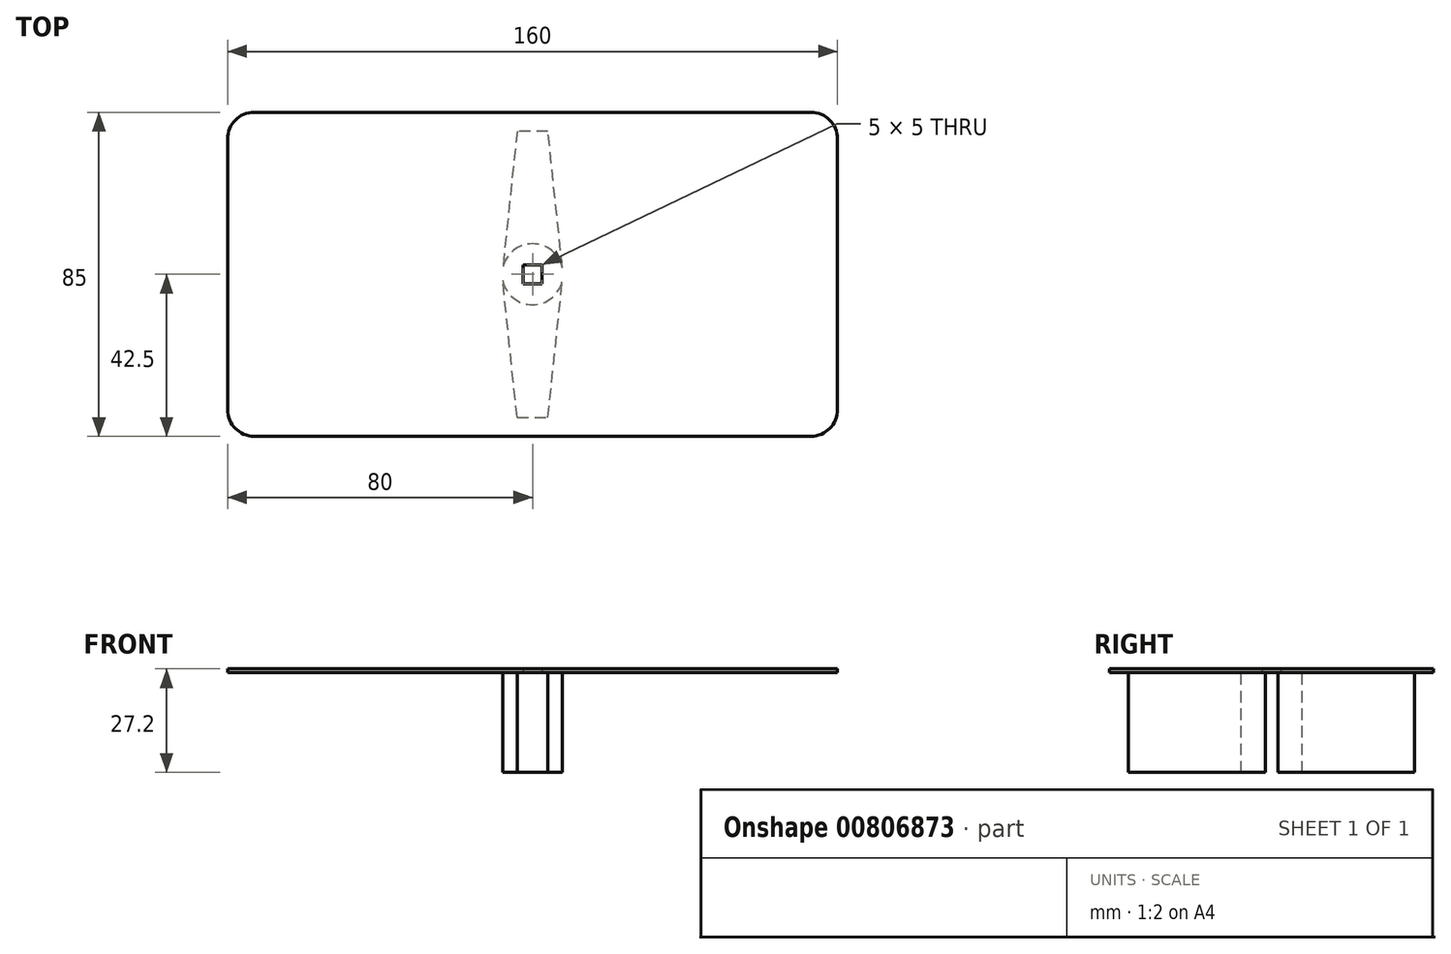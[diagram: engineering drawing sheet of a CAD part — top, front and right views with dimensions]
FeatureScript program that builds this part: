
annotation { "Feature Type Name" : "Feature", "Feature Type Description" : "" }
export const myFeature = defineFeature(function(context is Context, id is Id, definition is map)
    precondition{}
    {
        {
            var Q0;
            Q0=qCreatedBy(makeId("Top.planeOp"),FACE);
            var sketch = newSketch(context, id + "F0", { "sketchPlane" : qUnion([Q0])});
            skLineSegment(sketch, "E0.bottom", {"start": v(80, -42.5) * mm, "end": v(-80, -42.5) * mm});
            skLineSegment(sketch, "E0.top", {"start": v(80, 42.5) * mm, "end": v(-80, 42.5) * mm});
            skLineSegment(sketch, "E0.left", {"start": v(80, -42.5) * mm, "end": v(80, 42.5) * mm});
            skLineSegment(sketch, "E0.right", {"start": v(-80, -42.5) * mm, "end": v(-80, 42.5) * mm});
            skPoint(sketch, "E0.middle", {"position": v(0, 0) * mm});
            skCircle(sketch, "E1", {"center": v(0, 0) * mm, "radius": 8 * mm});
            skLineSegment(sketch, "E2", {"start": v(80, 42.5) * mm, "end": v(80, 35.5) * mm});
            skLineSegment(sketch, "E3", {"start": v(80, 42.5) * mm, "end": v(73, 42.5) * mm});
            skArc(sketch, "E4", {"start": v(80, 35.5) * mm, "mid": v(77.95, 40.45) * mm, "end": v(73, 42.5) * mm});
            skLineSegment(sketch, "E5", {"start": v(80, -42.5) * mm, "end": v(80, -35.5) * mm});
            skLineSegment(sketch, "E6", {"start": v(80, -42.5) * mm, "end": v(73, -42.5) * mm});
            skArc(sketch, "E7", {"start": v(73, -42.5) * mm, "mid": v(77.95, -40.45) * mm, "end": v(80, -35.5) * mm});
            skLineSegment(sketch, "E8", {"start": v(-80, -42.5) * mm, "end": v(-73, -42.5) * mm});
            skLineSegment(sketch, "E9", {"start": v(-80, -42.5) * mm, "end": v(-80, -35.5) * mm});
            skArc(sketch, "E10", {"start": v(-80, -35.5) * mm, "mid": v(-77.95, -40.45) * mm, "end": v(-73, -42.5) * mm});
            skLineSegment(sketch, "E11", {"start": v(-80, 42.5) * mm, "end": v(-80, 35.5) * mm});
            skLineSegment(sketch, "E12", {"start": v(-80, 42.5) * mm, "end": v(-73, 42.5) * mm});
            skArc(sketch, "E13", {"start": v(-73, 42.5) * mm, "mid": v(-77.95, 40.45) * mm, "end": v(-80, 35.5) * mm});
            skSolve(sketch);
        }
        {
            var Q0;
            Q0=makeQuery(id+"F0.imprint","IMPRINT",FACE,{"disambiguationData":[TD([[makeQuery(id+"F0.imprint","IMPRINT",EDGE,{"derivedFrom":sQuery(id+"F0.wireOp",EDGE,"E1")}),1.0]])]});
            var Q1;
            Q1=makeQuery(id+"F0.imprint","IMPRINT",FACE,{"disambiguationData":[TD([[makeQuery(id+"F0.imprint","IMPRINT",EDGE,{"derivedFrom":sQuery(id+"F0.wireOp",EDGE,"E1")}),-1.0]])]});
            extrude(context, id + "F1", {"entities" : qUnion([Q0, Q1]), "depth" : 1 * mm, "offsetDistance" : 25 * mm});
        }
        {
            var Q0;
            Q0=makeQuery(id+"F1.opExtrude","CAP_FACE",FACE,{"disambiguationData":[OSD([sQuery(id+"F0.wireOp",EDGE,"E0.bottom"),sQuery(id+"F0.wireOp",EDGE,"E0.top"),sQuery(id+"F0.wireOp",EDGE,"E0.left"),sQuery(id+"F0.wireOp",EDGE,"E0.right"),sQuery(id+"F0.wireOp",EDGE,"E4"),sQuery(id+"F0.wireOp",EDGE,"E7"),sQuery(id+"F0.wireOp",EDGE,"E10"),sQuery(id+"F0.wireOp",EDGE,"E13")])],"isStart":true});
            var sketch = newSketch(context, id + "F2", { "sketchPlane" : qUnion([Q0])});
            skCircle(sketch, "E14", {"center": v(0, 0) * mm, "radius": 8 * mm});
            skSolve(sketch);
        }
        {
            var Q0;
            Q0=makeQuery(id+"F1.opExtrude","CAP_FACE",FACE,{"disambiguationData":[OSD([sQuery(id+"F0.wireOp",EDGE,"E0.bottom"),sQuery(id+"F0.wireOp",EDGE,"E0.top"),sQuery(id+"F0.wireOp",EDGE,"E0.left"),sQuery(id+"F0.wireOp",EDGE,"E0.right"),sQuery(id+"F0.wireOp",EDGE,"E4"),sQuery(id+"F0.wireOp",EDGE,"E7"),sQuery(id+"F0.wireOp",EDGE,"E10"),sQuery(id+"F0.wireOp",EDGE,"E13")])],"isStart":true});
            var sketch = newSketch(context, id + "F3", { "sketchPlane" : qUnion([Q0])});
            skCircle(sketch, "E15", {"center": v(0, 0) * mm, "radius": 8 * mm});
            skLineSegment(sketch, "E16", {"start": v(-8, 0) * mm, "end": v(-8, 25) * mm});
            skLineSegment(sketch, "E17", {"start": v(8, 0) * mm, "end": v(8, 25) * mm});
            skLineSegment(sketch, "E18", {"start": v(8, 25) * mm, "end": v(-8, 25) * mm});
            skLineSegment(sketch, "E19", {"start": v(-8, 0) * mm, "end": v(-8, -15) * mm});
            skLineSegment(sketch, "E20", {"start": v(8, 0) * mm, "end": v(8, -15) * mm});
            skLineSegment(sketch, "E21", {"start": v(8, -15) * mm, "end": v(-8, -15) * mm});
            skLineSegment(sketch, "E22", {"start": v(3.08, -15) * mm, "end": v(4.02, -10.14) * mm});
            skLineSegment(sketch, "E23", {"start": v(8, 0) * mm, "end": v(3.48, -43) * mm});
            skLineSegment(sketch, "E24", {"start": v(8, -15) * mm, "end": v(8, -42.5) * mm});
            skLineSegment(sketch, "E25", {"start": v(8, -42.5) * mm, "end": v(3.53, -42.5) * mm});
            skLineSegment(sketch, "E26", {"start": v(8, 25) * mm, "end": v(8, 42.5) * mm});
            skLineSegment(sketch, "E27", {"start": v(8, 42.5) * mm, "end": v(3.53, 42.5) * mm});
            skLineSegment(sketch, "E28", {"start": v(3.53, 42.5) * mm, "end": v(8, 0) * mm});
            skLineSegment(sketch, "E29", {"start": v(-8, 25) * mm, "end": v(-8, 42.5) * mm});
            skLineSegment(sketch, "E30", {"start": v(-8, 42.5) * mm, "end": v(-3.53, 42.5) * mm});
            skLineSegment(sketch, "E31", {"start": v(-3.53, 42.5) * mm, "end": v(-8, 0) * mm});
            skLineSegment(sketch, "E32", {"start": v(-8, -15) * mm, "end": v(-8, -42.5) * mm});
            skLineSegment(sketch, "E33", {"start": v(-8, -42.5) * mm, "end": v(-3.53, -42.5) * mm});
            skLineSegment(sketch, "E34", {"start": v(-3.53, -42.5) * mm, "end": v(-8, 0) * mm});
            skLineSegment(sketch, "E35", {"start": v(-8, -42.5) * mm, "end": v(-8, -37.5) * mm});
            skLineSegment(sketch, "E36", {"start": v(8, -42.5) * mm, "end": v(8, -37.5) * mm});
            skLineSegment(sketch, "E37", {"start": v(8, -37.5) * mm, "end": v(-8, -37.5) * mm});
            skLineSegment(sketch, "E38", {"start": v(8, 42.5) * mm, "end": v(8, 37.5) * mm});
            skLineSegment(sketch, "E39", {"start": v(-8, 42.5) * mm, "end": v(-8, 37.5) * mm});
            skLineSegment(sketch, "E40", {"start": v(-8, 37.5) * mm, "end": v(8, 37.5) * mm});
            skLineSegment(sketch, "E41", {"start": v(-8, 1.41) * mm, "end": v(-8, -1.52) * mm});
            skLineSegment(sketch, "E42", {"start": v(8, 2.1) * mm, "end": v(8, -1.7) * mm});
            skSolve(sketch);
        }
        {
            var Q0;
            Q0=makeQuery(id+"F1.opExtrude","CAP_FACE",FACE,{"disambiguationData":[OSD([sQuery(id+"F0.wireOp",EDGE,"E0.bottom"),sQuery(id+"F0.wireOp",EDGE,"E0.top"),sQuery(id+"F0.wireOp",EDGE,"E0.left"),sQuery(id+"F0.wireOp",EDGE,"E0.right"),sQuery(id+"F0.wireOp",EDGE,"E4"),sQuery(id+"F0.wireOp",EDGE,"E7"),sQuery(id+"F0.wireOp",EDGE,"E10"),sQuery(id+"F0.wireOp",EDGE,"E13")])],"isStart":true});
            var sketch = newSketch(context, id + "F4", { "sketchPlane" : qUnion([Q0])});
            skLineSegment(sketch, "E43.bottom", {"start": v(2.5, -2.5) * mm, "end": v(-2.5, -2.5) * mm});
            skLineSegment(sketch, "E43.top", {"start": v(2.5, 2.5) * mm, "end": v(-2.5, 2.5) * mm});
            skLineSegment(sketch, "E43.left", {"start": v(2.5, -2.5) * mm, "end": v(2.5, 2.5) * mm});
            skLineSegment(sketch, "E43.right", {"start": v(-2.5, -2.5) * mm, "end": v(-2.5, 2.5) * mm});
            skPoint(sketch, "E43.middle", {"position": v(0, 0) * mm});
            skSolve(sketch);
        }
        {
            var Q0;
            Q0 = qSketchRegion(id + "F4", true);
            extrude(context, id + "F5", {"entities" : qUnion([Q0]), "operationType" : NewBodyOperationType.REMOVE, "oppositeDirection" : true, "depth" : 25 * mm, "offsetDistance" : 25 * mm});
        }
        {
            var Q0;
            {var subQ0=sQuery(id+"F3.wireOp",EDGE,"E28");var subQ1=sQuery(id+"F3.wireOp",EDGE,"E15");var subQ2=makeQuery(id+"F3.imprint","INTERSECT",VERTEX,{"derivedFrom":[subQ1,subQ0]});Q0=makeQuery(id+"F3.imprint","IMPRINT",FACE,{"disambiguationData":[TD([[makeQuery(id+"F3.imprint","IMPRINT",EDGE,{"disambiguationData":[TD([[subQ2,-1.0]])],"derivedFrom":subQ1}),-1.0]])]});}
            var Q1;
            {var subQ0=sQuery(id+"F3.wireOp",EDGE,"E28");var subQ1=sQuery(id+"F3.wireOp",EDGE,"E18");var subQ2=makeQuery(id+"F3.imprint","INTERSECT",VERTEX,{"derivedFrom":[subQ1,subQ0]});Q1=makeQuery(id+"F3.imprint","IMPRINT",FACE,{"disambiguationData":[TD([[makeQuery(id+"F3.imprint","IMPRINT",EDGE,{"disambiguationData":[TD([[subQ2,-1.0]])],"derivedFrom":subQ1}),-1.0]])]});}
            var Q2;
            {var subQ0=sQuery(id+"F3.wireOp",EDGE,"E21");var subQ1=makeQuery(id+"F3.imprint","IMPRINT",VERTEX,{"derivedFrom":subQ0});Q2=makeQuery(id+"F3.imprint","IMPRINT",FACE,{"disambiguationData":[TD([[makeQuery(id+"F3.imprint","IMPRINT",EDGE,{"disambiguationData":[TD([[subQ1,-1.0]])],"derivedFrom":subQ0}),-1.0]])]});}
            var Q3;
            {var subQ3=sQuery(id+"F3.wireOp",EDGE,"E21");var subQ8=makeQuery(id+"F3.imprint","IMPRINT",VERTEX,{"derivedFrom":subQ3});Q3=makeQuery(id+"F3.imprint","IMPRINT",FACE,{"disambiguationData":[TD([[makeQuery(id+"F3.imprint","IMPRINT",EDGE,{"disambiguationData":[TD([[subQ8,-1.0]])],"derivedFrom":subQ3}),1.0]])]});}
            extrude(context, id + "F6", {"entities" : qUnion([Q0, Q1, Q2, Q3]), "operationType" : NewBodyOperationType.ADD, "depth" : 26.2 * mm, "offsetDistance" : 25 * mm});
        }
    });
